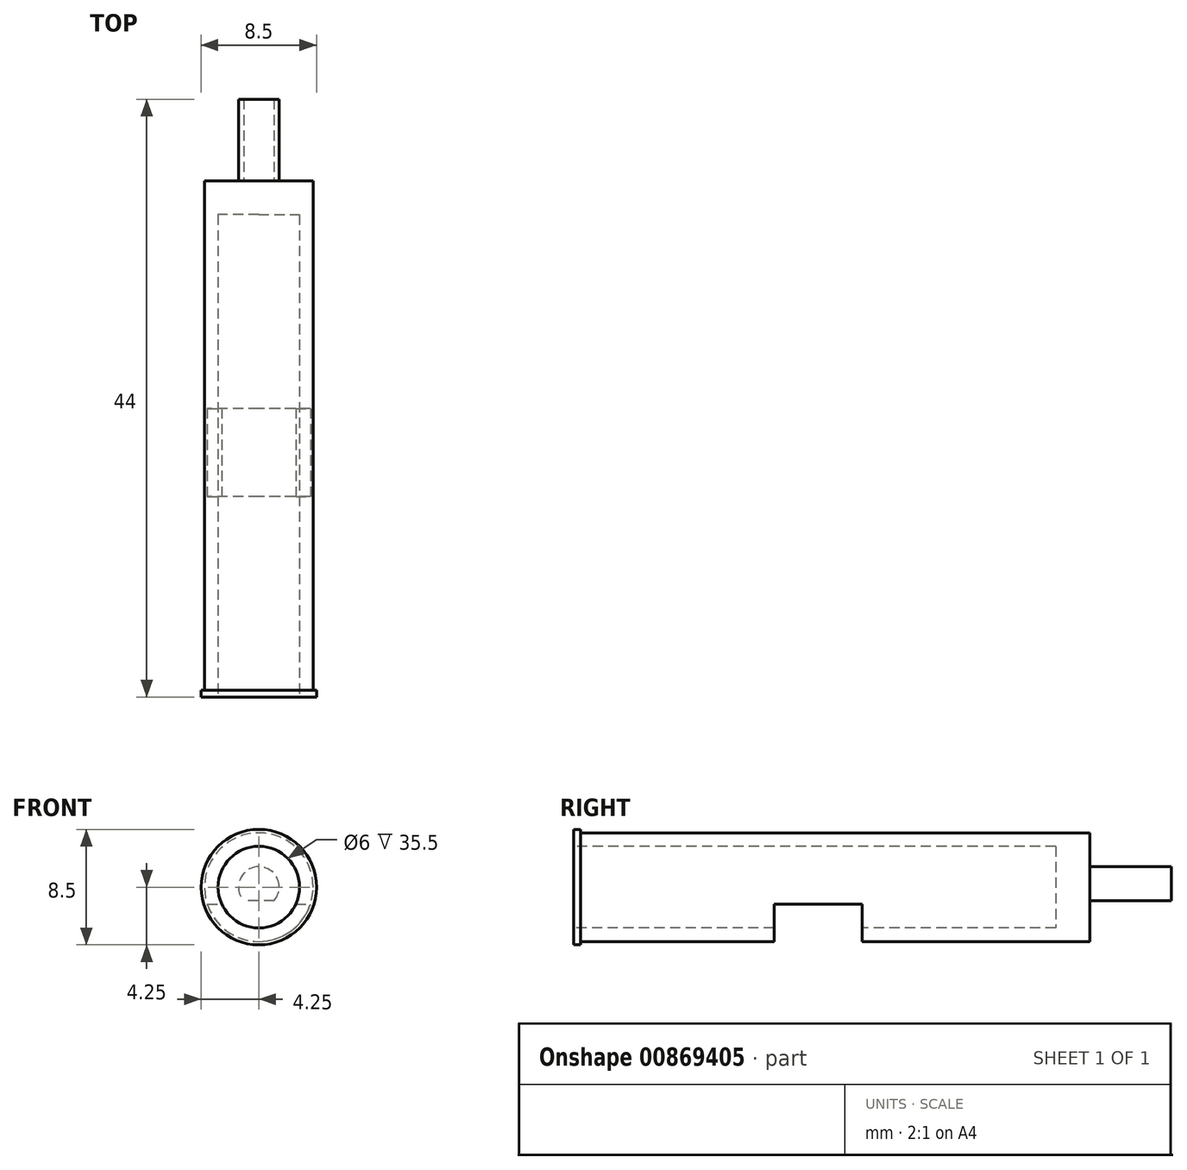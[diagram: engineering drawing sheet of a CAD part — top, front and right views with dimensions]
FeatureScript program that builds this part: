
annotation { "Feature Type Name" : "Feature", "Feature Type Description" : "" }
export const myFeature = defineFeature(function(context is Context, id is Id, definition is map)
    precondition{}
    {
        {
            var Q0;
            Q0=qCreatedBy(makeId("Front.planeOp"),FACE);
            var sketch = newSketch(context, id + "F0", { "sketchPlane" : qUnion([Q0])});
            skCircle(sketch, "E0", {"center": v(0, 0) * mm, "radius": 4 * mm});
            skCircle(sketch, "E1", {"center": v(0, 0) * mm, "radius": 3 * mm});
            skSolve(sketch);
        }
        {
            var Q0;
            Q0 = qSketchRegion(id + "F0", true);
            extrude(context, id + "F1", {"entities" : qUnion([Q0]), "oppositeDirection" : true, "depth" : 38 * mm, "offsetDistance" : 25 * mm});
        }
        {
            var Q0;
            Q0=makeQuery(id+"F1.opExtrude","CAP_FACE",FACE,{"disambiguationData":[OSD([sQuery(id+"F0.wireOp",EDGE,"E0"),sQuery(id+"F0.wireOp",EDGE,"E1")])],"isStart":true});
            var sketch = newSketch(context, id + "F2", { "sketchPlane" : qUnion([Q0])});
            skCircle(sketch, "E2", {"center": v(0, 0) * mm, "radius": 4.25 * mm});
            skCircle(sketch, "E3.0", {"center": v(0, 0) * mm, "radius": 3 * mm});
            skSolve(sketch);
        }
        {
            var Q0;
            Q0=makeQuery(id+"F2.imprint","IMPRINT",FACE,{"disambiguationData":[TD([[makeQuery(id+"F2.imprint","IMPRINT",EDGE,{"derivedFrom":sQuery(id+"F2.wireOp",EDGE,"E2")}),1.0]])]});
            var Q1;
            Q1=makeQuery(id+"F2.imprint","IMPRINT",FACE,{"disambiguationData":[TD([[makeQuery(id+"F2.imprint","IMPRINT",EDGE,{"derivedFrom":sQuery(id+"F2.wireOp",EDGE,"E3.0")}),-1.0]])]});
            extrude(context, id + "F3", {"entities" : qUnion([Q0, Q1]), "operationType" : NewBodyOperationType.ADD, "oppositeDirection" : true, "depth" : .5 * mm, "offsetDistance" : 25 * mm});
        }
        {
            var Q0;
            Q0=qCreatedBy(makeId("Right.planeOp"),FACE);
            var sketch = newSketch(context, id + "F4", { "sketchPlane" : qUnion([Q0])});
            skLineSegment(sketch, "E4", {"start": v(21.24, -4) * mm, "end": v(14.75, -4) * mm});
            skLineSegment(sketch, "E5.top", {"start": v(21.24, -1.25) * mm, "end": v(14.75, -1.25) * mm});
            skLineSegment(sketch, "E5.left", {"start": v(21.24, -4) * mm, "end": v(21.24, -1.25) * mm});
            skLineSegment(sketch, "E5.right", {"start": v(14.75, -4) * mm, "end": v(14.75, -1.25) * mm});
            skSolve(sketch);
        }
        {
            var Q0;
            Q0=makeQuery(id+"F4.imprint","IMPRINT",FACE,{"disambiguationData":[TD([[makeQuery(id+"F4.imprint","IMPRINT",EDGE,{"derivedFrom":sQuery(id+"F4.wireOp",EDGE,"E4")}),-1.0]])]});
            extrude(context, id + "F5", {"entities" : qUnion([Q0]), "operationType" : NewBodyOperationType.REMOVE, "endBound" : BoundingType.SYMMETRIC, "oppositeDirection" : true, "depth" : 25 * mm, "offsetDistance" : 25 * mm});
        }
        {
            var Q0;
            Q0=makeQuery(id+"F1.opExtrude","CAP_FACE",FACE,{"disambiguationData":[OSD([sQuery(id+"F0.wireOp",EDGE,"E0"),sQuery(id+"F0.wireOp",EDGE,"E1")])],"isStart":false});
            var sketch = newSketch(context, id + "F6", { "sketchPlane" : qUnion([Q0])});
            skCircle(sketch, "E6.0", {"center": v(0, 0) * mm, "radius": 4 * mm});
            skSolve(sketch);
        }
        {
            var Q0;
            Q0=makeQuery(id+"F6.imprint","IMPRINT",FACE,{"disambiguationData":[TD([[makeQuery(id+"F6.imprint","IMPRINT",EDGE,{"derivedFrom":sQuery(id+"F6.wireOp",EDGE,"E6.0")}),-1.0]])]});
            var Q1;
            Q1=makeQuery(id+"F6.imprint","IMPRINT",FACE,{"disambiguationData":[TD([[makeQuery(id+"F6.imprint","IMPRINT",EDGE,{"derivedFrom":makeQuery(id+"F1.opExtrude","CAP_EDGE",EDGE,{"disambiguationData":[OSD([sQuery(id+"F0.wireOp",EDGE,"E1")])],"isStart":false})}),-1.0]])]});
            extrude(context, id + "F7", {"entities" : qUnion([Q0, Q1]), "operationType" : NewBodyOperationType.ADD, "oppositeDirection" : true, "depth" : 2.5 * mm, "offsetDistance" : 25 * mm});
        }
        {
            var Q0;
            Q0=makeQuery(id+"F7.boolean.opBoolean","MERGE",FACE,{"derivedFrom":[makeQuery(id+"F1.opExtrude","CAP_FACE",FACE,{"disambiguationData":[OSD([sQuery(id+"F0.wireOp",EDGE,"E0"),sQuery(id+"F0.wireOp",EDGE,"E1")])],"isStart":false}),makeQuery(id+"F7.opExtrude","CAP_FACE",FACE,{"disambiguationData":[OSD([sQuery(id+"F6.wireOp",EDGE,"E6.0")])],"isStart":true})]});
            var sketch = newSketch(context, id + "F8", { "sketchPlane" : qUnion([Q0])});
            skArc(sketch, "E7", {"start": v(1.12, -1) * mm, "mid": v(0, 1.5) * mm, "end": v(-1.12, -1) * mm});
            skLineSegment(sketch, "E8", {"start": v(-1.12, -1) * mm, "end": v(1.12, -1) * mm});
            skSolve(sketch);
        }
        {
            var Q0;
            Q0=makeQuery(id+"F8.imprint","IMPRINT",FACE,{"disambiguationData":[TD([[makeQuery(id+"F8.imprint","IMPRINT",EDGE,{"derivedFrom":sQuery(id+"F8.wireOp",EDGE,"E7")}),1.0]])]});
            extrude(context, id + "F9", {"entities" : qUnion([Q0]), "operationType" : NewBodyOperationType.ADD, "depth" : 6 * mm, "offsetDistance" : 25 * mm});
        }
    });
